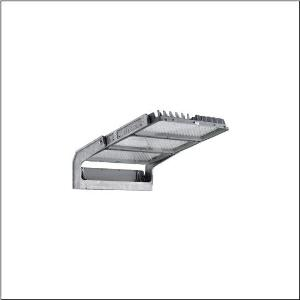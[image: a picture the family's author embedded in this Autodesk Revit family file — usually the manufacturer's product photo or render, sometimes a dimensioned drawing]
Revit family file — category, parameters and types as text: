
# Revit family: floodlight_fl_11_maxi_pro___rs07_5xa779128k02fb_ed38
name_source: partatom
category: Lighting Fixtures
units: mm (PartAtom-declared; Revit-internal decimal feet)

## family parameters
Cut with Voids When Loaded = No
Host = Face
Light Source = No
Part Type = Normal
Room Calculation Point = No
Round Connector Dimension = Use Diameter
Shared = No

## types (1)
- --- (1 x LED, 157630 lm, 1368.3 W, 5700K)
    Apparent Load = 1368 VA
    CIE Flux Codes = 80 93 99 100 99
    Color Rendering = 80
    Color Temperature = 5700K
    Default Elevation = 1800 mm
    Description = Floodlight FL 11  maxi  pro floodlight; light control with lens of PMMA; cover panel of toughened safety glass, transparent; light distribution: RS07, rotationally symmetric direct distribution, LED; colour temperature: 5700K, rated luminous flux: 157.630lm, colour rendering: CRI > 80, light colour: 857; luminous efficacy: 115lm/W; brightness control: DALI 2; with terminal, 5-pole, max. 2.5mm², mains connection: 220..240V/380..400V AC, 50/60Hz, surge voltage resistance: line to ground: 10kV, LED service life up to 100,000h L90. Typical operating time: 1000h per year., ECG replaceable separately, LED unit replaceable without ESD environment, dustproof LED module, dimming range 10..100%; 1368W floodlight with 3x LED unit of diecast aluminium, coated grey; length: 1.003mm / width: 651mm / height: 338mm; mounting bracket, of diecast aluminium, uncoated, natural, equipment: Power, protection rating (complete): IP66; insulation class (complete): insulation class I (protective earthing); certification: CE, ENEC, VDE; ball protection: ball impact resistant, only for outdoor installations in the designated locations, permissible operating ambient temperature: -45..+55°C, permissible storage temperature: -40..+85°Cpackaging unit: 1 piece

Light Distribution: RS07
    Height = 320 mm
    Lamp = 1 x LED
    Lamp Light Flux = 157630 lm
    Lamp Power = 1368.3 W
    Lamp count = 1
    Length = 1002 mm
    Luminous efficacy = 115 lm/W
    Manufacturer = Siteco
    ModVariant = No
    Model = 5XA779128K02FB
    Mounting Place = Ceiling
    Mounting Type = Surface mounted
    Number of Poles = 1
    OnlyDefault = Yes
    Power Factor = 1
    Product Name = Floodlight FL 11 maxi pro | RS07
    Product group = floodlight | ceiling mounted
    ProductGroupID = 303
    Protection Class = Protection class I
    Protection Degree = IP 66
    RLX_Detail_Level = 1
    RLX_Emergency_Light_Flux = 0 lm
    RLX_Emergency_Type = 0
    RLX_Emergency_Type_DB = No
    RlxData = <blob elided: 40273 chars, md5=87beb04a>
    Socket = socket
    Standby Power = 0 W
    System Light Flux = 157630 lm
    System Power = 1368 W
    Type Comments = factory setting: luminous flux: 100 % | dim-lin: 254 | 935 mA
    Type Image = l_1356210.jpg
    URL = http://relux.com
    VarID = @adj_038675
    Voltage = 0 V
    Weight = 0.00 kg
    Width = 655 mm

## geometry (parser evidence)
native form markers: Blend x4, Sweep x12
no freeform markers — native parametric forms only
